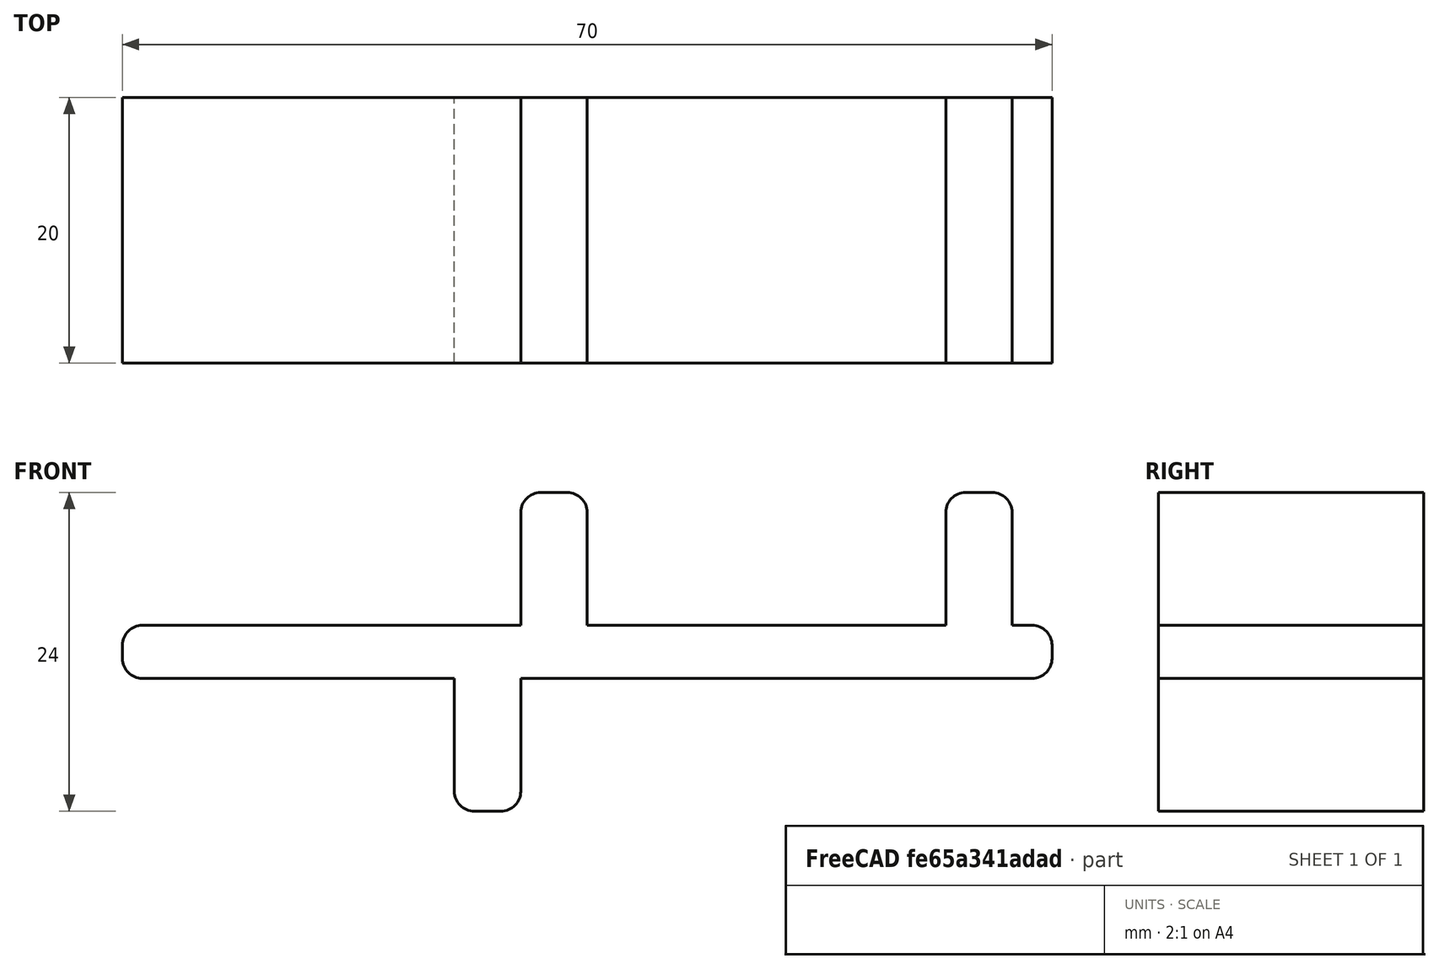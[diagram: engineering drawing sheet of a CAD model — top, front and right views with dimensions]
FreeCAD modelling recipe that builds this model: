
FCSTD DOCUMENT  (FreeCAD 0.21R33771 (Git))
Label: picture_stand_bigger
License: All rights reserved
LicenseURL: http://en.wikipedia.org/wiki/All_rights_reserved
objects: Part::Box×4, Part::Fillet×3, Spreadsheet::Sheet×1, Part::Cut×1, Part::MultiFuse×1, App::Part×1
note: 9 computed .brp shape members not serialized (recipe doc carries the construction recipe); baked Part::Feature solids carry a one-line shape summary decoded from their .brp

FEATURE [Part::Box] Box  label="Cube"
  AttacherType = Attacher::AttachEngine3D
  Height = 4
  Length = 70
  Width = 20
  expr: Length = <<p>>.length
  expr: Width = <<p>>.width
FEATURE [Part::Box] Box001  label="Cube001"
  AttacherType = Attacher::AttachEngine3D
  Height = 10
  Length = 37
  Placement = pos=(30,0,4) rot=(0,0,1;0rad)
  Width = 20
  expr: Width = <<p>>.width
FEATURE [Part::Box] Box002  label="Cube002"
  AttacherType = Attacher::AttachEngine3D
  Height = 10
  Length = 27
  Placement = pos=(35,0,4) rot=(0,0,1;0rad)
  Width = 20
  expr: .Placement.Base.x = <<Cube001>>.Placement.Base.x + 5 mm
  expr: Width = <<p>>.width
FEATURE [Spreadsheet::Sheet] Spreadsheet  label="p"
  cells = A1='width; B1(width)=20; A2='length; B2(length)=70
FEATURE [Part::Fillet] Fillet
  Base = -> Box
  Edges = 4 edges r=1.5: [Edge2,Edge4,Edge6,Edge8]
FEATURE [Part::Cut] Cut001
  Base = -> Box001
  Tool = -> Box002
FEATURE [Part::Fillet] Fillet001
  Base = -> Cut001
  Edges = 4 edges r=1.5: [Edge2,Edge9,Edge20,Edge23]
FEATURE [Part::Box] Box003  label="Cube003"
  AttacherType = Attacher::AttachEngine3D
  Height = 10
  Length = 5
  Placement = pos=(25,0,-10) rot=(0,0,1;0rad)
  Width = 20
  expr: Width = <<p>>.width
FEATURE [Part::Fillet] Fillet002
  Base = -> Box003
  Edges = 2 edges r=1.5: [Edge4,Edge8]
FEATURE [Part::MultiFuse] Fusion
  Shapes = -> [Fillet,Fillet001,Fillet002]
FEATURE [App::Part] Part
  Group = -> [Box,Fusion,Fillet]
  Origin = -> Origin
